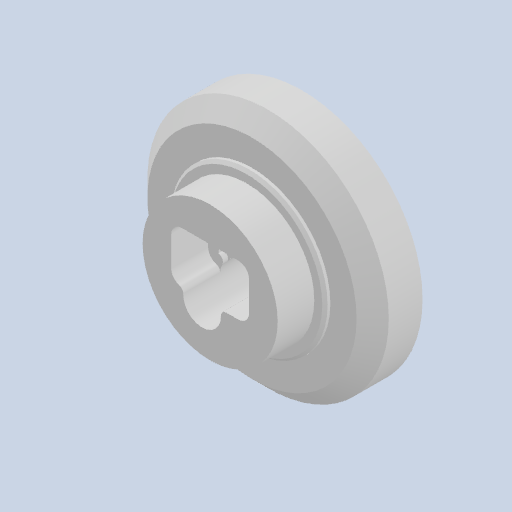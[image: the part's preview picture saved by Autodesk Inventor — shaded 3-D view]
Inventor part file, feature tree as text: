
AUTODESK INVENTOR PART (.ipt)
format: ipt  version: 2022 (Build 260153000, 153)  size: 219,648 bytes
history: native  units: mm
features: extrude x8, sketch x8, other x4, projected_geometry x4, reference x4, chamfer x2, fillet x2
ambient origin geometry x8: Origin, YZ Plane, XZ Plane, XY Plane, X Axis, Y Axis, Z Axis, Center Point
bodies: Body1 (feature_tree)
feature tree (32):
  other  "Твердое тело1"
  extrude  "Выдавливание1"  Depth=45.0mm
  extrude  "Выдавливание2"  Depth=9.295mm TaperAngle=0.0deg
  extrude  "Выдавливание3"  Depth=25.2mm
  chamfer  "Фаска1"  Distance=7.8mm
  extrude  "Выдавливание4"  Depth=2.0mm
  extrude  "Выдавливание5"  Depth=1.0mm TaperAngle=0.0deg
  extrude  "Выдавливание6"  Depth=2.0mm TaperAngle=45.0deg
  extrude  "Выдавливание7"  Depth=7.8mm TaperAngle=0.0deg
  chamfer  "Фаска2"  Distance=4.2mm
  extrude  "Выдавливание10"  Depth=4.2mm
  fillet  "Сопряжение3"  Radius=4.2mm
  fillet  "Сопряжение4"  Radius=7.8mm
  sketch  "Эскиз1"
  sketch  "Эскиз2"
  sketch  "Эскиз3"
  projected_geometry  "Спроецированная петля1"
  sketch  "Эскиз4"
  sketch  "Эскиз5"
  reference  "Ссылка1"
  reference  "Ссылка2"
  reference  "Ссылка3"
  sketch  "Эскиз6"
  reference  "Ссылка4"
  sketch  "Эскиз7"
  sketch  "Эскиз10"
  projected_geometry  "Спроецированная петля3"
  projected_geometry  "Спроецированная петля4"
  projected_geometry  "Спроецированная петля5"
  other  "<userpath>\Documents\Git\MZCAT_2024\MZCAT.iam"
  other  "MZCAT.iam"
  other  "base plate:2"
